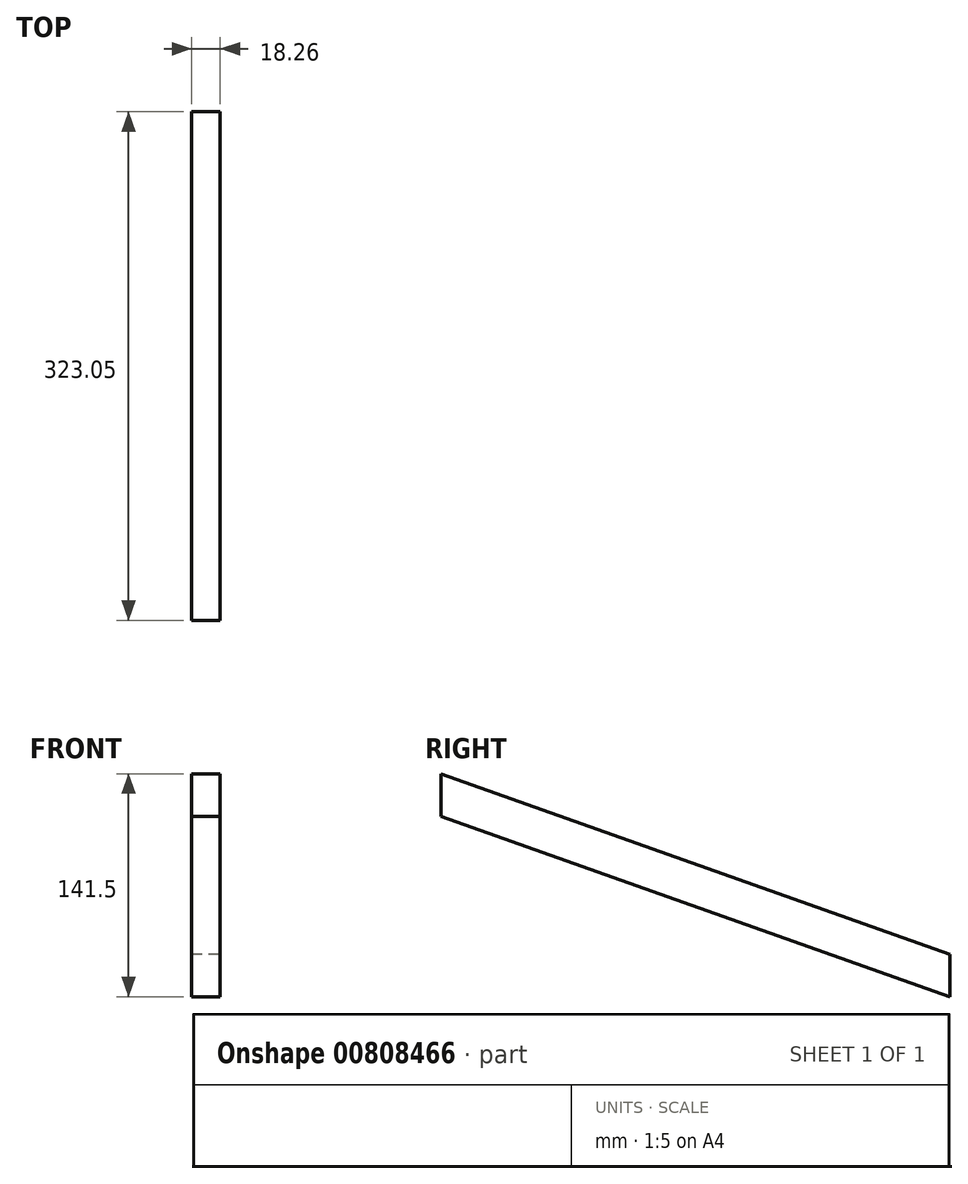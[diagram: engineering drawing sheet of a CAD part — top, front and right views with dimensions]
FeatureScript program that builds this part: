
annotation { "Feature Type Name" : "Feature", "Feature Type Description" : "" }
export const myFeature = defineFeature(function(context is Context, id is Id, definition is map)
    precondition{}
    {
        {
            var Q0;
            Q0=qCreatedBy(makeId("Right.planeOp"),FACE);
            var sketch = newSketch(context, id + "F0", { "sketchPlane" : qUnion([Q0])});
            skLineSegment(sketch, "E0", {"start": v(-138.66, -12.75) * mm, "end": v(-138.66, -114.35) * mm});
            skLineSegment(sketch, "E1", {"start": v(-138.66, -114.35) * mm, "end": v(147.88, -114.35) * mm});
            skLineSegment(sketch, "E2", {"start": v(147.88, -114.35) * mm, "end": v(-138.66, -12.75) * mm});
            skSolve(sketch);
        }
        {
            var Q0;
            Q0=qCreatedBy(makeId("Right.planeOp"),FACE);
            var sketch = newSketch(context, id + "F1", { "sketchPlane" : qUnion([Q0])});
            skLineSegment(sketch, "E3", {"start": v(-35.75, 12.33) * mm, "end": v(-35.75, -14.62) * mm});
            skLineSegment(sketch, "E4", {"start": v(-35.75, -14.62) * mm, "end": v(287.3, -129.17) * mm});
            skLineSegment(sketch, "E5", {"start": v(287.3, -129.17) * mm, "end": v(287.3, -102.22) * mm});
            skLineSegment(sketch, "E6", {"start": v(287.3, -102.22) * mm, "end": v(-35.75, 12.33) * mm});
            skSolve(sketch);
        }
        {
            var Q0;
            Q0 = qSketchRegion(id + "F1", true);
            extrude(context, id + "F2", {"entities" : qUnion([Q0]), "depth" : 18.26 * mm, "offsetDistance" : 25.4 * mm});
        }
    });
